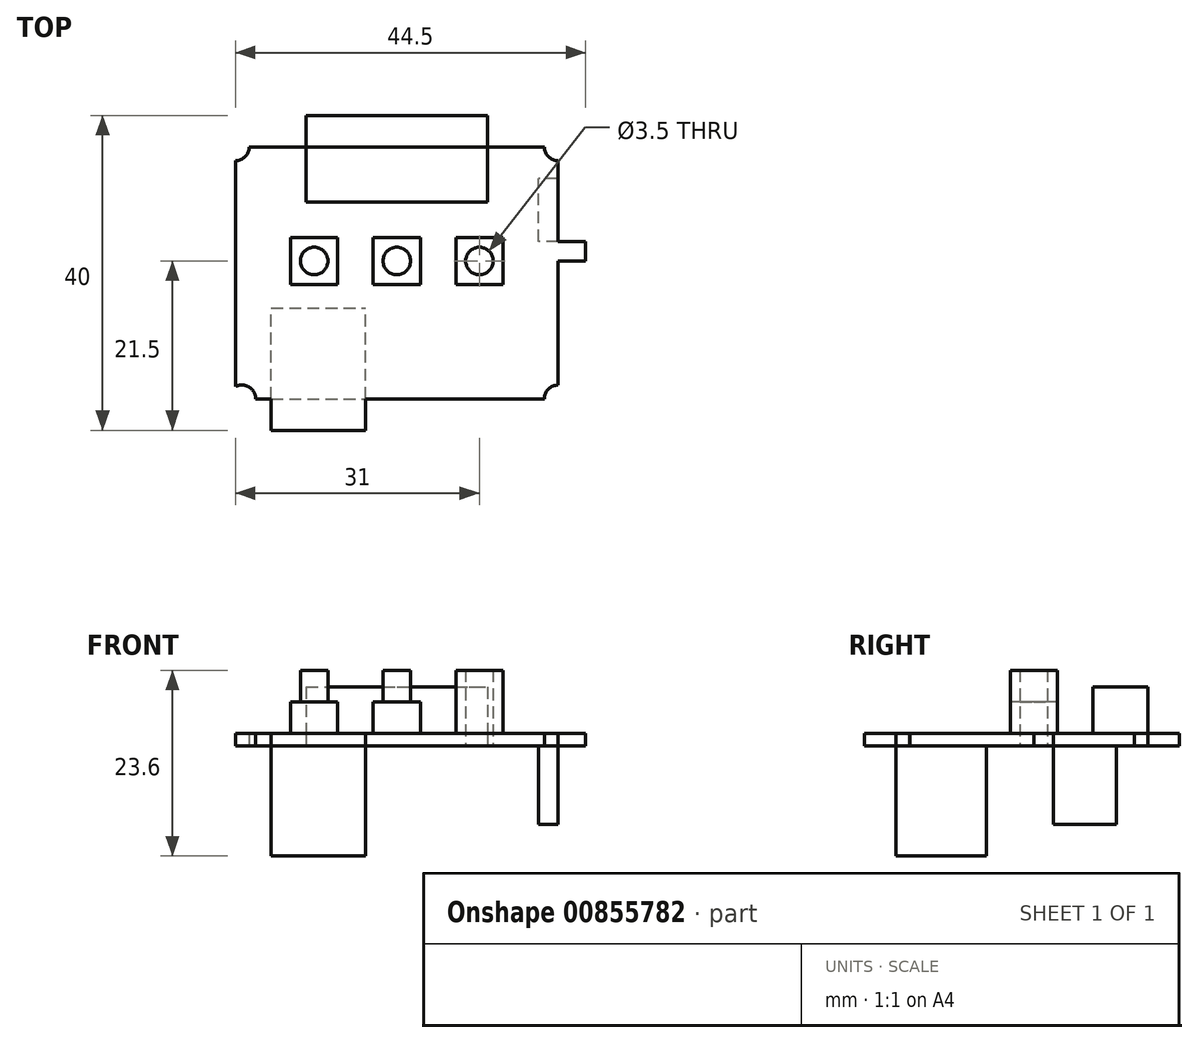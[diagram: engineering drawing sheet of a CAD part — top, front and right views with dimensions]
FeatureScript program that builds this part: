
annotation { "Feature Type Name" : "Feature", "Feature Type Description" : "" }
export const myFeature = defineFeature(function(context is Context, id is Id, definition is map)
    precondition{}
    {
        {
            var Q0;
            Q0=qCreatedBy(makeId("Top.planeOp"),FACE);
            var sketch = newSketch(context, id + "F0", { "sketchPlane" : qUnion([Q0])});
            skLineSegment(sketch, "E0.bottom", {"start": v(-20.5, 16) * mm, "end": v(20.5, 16) * mm});
            skLineSegment(sketch, "E0.top", {"start": v(-20.5, -16) * mm, "end": v(20.5, -16) * mm});
            skLineSegment(sketch, "E0.left", {"start": v(-20.5, 16) * mm, "end": v(-20.5, -16) * mm});
            skLineSegment(sketch, "E0.right", {"start": v(20.5, 16) * mm, "end": v(20.5, -16) * mm});
            skPoint(sketch, "E0.middle", {"position": v(0, 0) * mm});
            skLineSegment(sketch, "E1.bottom", {"start": v(-24, 20) * mm, "end": v(24, 20) * mm});
            skLineSegment(sketch, "E1.top", {"start": v(-24, -20) * mm, "end": v(24, -20) * mm});
            skLineSegment(sketch, "E1.left", {"start": v(-24, 20) * mm, "end": v(-24, -20) * mm});
            skLineSegment(sketch, "E1.right", {"start": v(24, 20) * mm, "end": v(24, -20) * mm});
            skCircle(sketch, "E2", {"center": v(-20.5, 16) * mm, "radius": 1.75 * mm});
            skCircle(sketch, "E3", {"center": v(20.5, 16) * mm, "radius": 1.75 * mm});
            skCircle(sketch, "E4", {"center": v(20.5, -16) * mm, "radius": 1.75 * mm});
            skCircle(sketch, "E5", {"center": v(-19.68, -16) * mm, "radius": 1.75 * mm});
            skLineSegment(sketch, "E6.bottom", {"start": v(-11.5, 20) * mm, "end": v(11.5, 20) * mm});
            skLineSegment(sketch, "E6.top", {"start": v(-11.5, 9) * mm, "end": v(11.5, 9) * mm});
            skLineSegment(sketch, "E6.left", {"start": v(-11.5, 20) * mm, "end": v(-11.5, 9) * mm});
            skLineSegment(sketch, "E6.right", {"start": v(11.5, 20) * mm, "end": v(11.5, 9) * mm});
            skLineSegment(sketch, "E7", {"start": v(-24, 1.5) * mm, "end": v(24, 1.5) * mm});
            skCircle(sketch, "E8", {"center": v(0, 1.5) * mm, "radius": 1.75 * mm});
            skCircle(sketch, "E9", {"center": v(-10.5, 1.5) * mm, "radius": 1.75 * mm});
            skCircle(sketch, "E10", {"center": v(10.5, 1.5) * mm, "radius": 1.75 * mm});
            skLineSegment(sketch, "E11.bottom", {"start": v(-13.5, 4.5) * mm, "end": v(-7.5, 4.5) * mm});
            skLineSegment(sketch, "E11.top", {"start": v(-13.5, -1.5) * mm, "end": v(-7.5, -1.5) * mm});
            skLineSegment(sketch, "E11.left", {"start": v(-13.5, 4.5) * mm, "end": v(-13.5, -1.5) * mm});
            skLineSegment(sketch, "E11.right", {"start": v(-7.5, 4.5) * mm, "end": v(-7.5, -1.5) * mm});
            skLineSegment(sketch, "E12.bottom", {"start": v(-3, 4.5) * mm, "end": v(3, 4.5) * mm});
            skLineSegment(sketch, "E12.top", {"start": v(-3, -1.5) * mm, "end": v(3, -1.5) * mm});
            skLineSegment(sketch, "E12.left", {"start": v(-3, 4.5) * mm, "end": v(-3, -1.5) * mm});
            skLineSegment(sketch, "E12.right", {"start": v(3, 4.5) * mm, "end": v(3, -1.5) * mm});
            skLineSegment(sketch, "E13.bottom", {"start": v(7.5, 4.5) * mm, "end": v(13.5, 4.5) * mm});
            skLineSegment(sketch, "E13.top", {"start": v(7.5, -1.5) * mm, "end": v(13.5, -1.5) * mm});
            skLineSegment(sketch, "E13.left", {"start": v(7.5, 4.5) * mm, "end": v(7.5, -1.5) * mm});
            skLineSegment(sketch, "E13.right", {"start": v(13.5, 4.5) * mm, "end": v(13.5, -1.5) * mm});
            skLineSegment(sketch, "E14.bottom", {"start": v(-15.95, -20) * mm, "end": v(-3.95, -20) * mm});
            skLineSegment(sketch, "E14.top", {"start": v(-15.95, -4.5) * mm, "end": v(-3.95, -4.5) * mm});
            skLineSegment(sketch, "E14.left", {"start": v(-15.95, -20) * mm, "end": v(-15.95, -4.5) * mm});
            skLineSegment(sketch, "E14.right", {"start": v(-3.95, -20) * mm, "end": v(-3.95, -4.5) * mm});
            skLineSegment(sketch, "E15.bottom", {"start": v(24, 4) * mm, "end": v(18, 4) * mm});
            skLineSegment(sketch, "E15.top", {"start": v(24, 12) * mm, "end": v(18, 12) * mm});
            skLineSegment(sketch, "E15.left", {"start": v(24, 4) * mm, "end": v(24, 12) * mm});
            skLineSegment(sketch, "E15.right", {"start": v(18, 4) * mm, "end": v(18, 12) * mm});
            skSolve(sketch);
        }
        {
            var Q0;
            {var subQ5=sQuery(id+"F0.wireOp",EDGE,"E2");var subQ10=sQuery(id+"F0.wireOp",EDGE,"E0.bottom");var subQ15=makeQuery(id+"F0.imprint","INTERSECT",VERTEX,{"derivedFrom":[subQ10,subQ5]});Q0=makeQuery(id+"F0.imprint","IMPRINT",FACE,{"disambiguationData":[TD([[makeQuery(id+"F0.imprint","IMPRINT",EDGE,{"disambiguationData":[TD([[subQ15,-1.0]])],"derivedFrom":subQ10}),-1.0]])]});}
            var Q1;
            Q1=makeQuery(id+"F0.imprint","IMPRINT",FACE,{"disambiguationData":[TD([[makeQuery(id+"F0.imprint","IMPRINT",EDGE,{"derivedFrom":sQuery(id+"F0.wireOp",EDGE,"E1.bottom")}),-1.0]])]});
            var Q2;
            {var subQ0=sQuery(id+"F0.wireOp",EDGE,"E11.top");Q2=makeQuery(id+"F0.imprint","IMPRINT",FACE,{"disambiguationData":[TD([[makeQuery(id+"F0.imprint","IMPRINT",EDGE,{"derivedFrom":subQ0}),-1.0]])]});}
            var Q3;
            {var subQ0=sQuery(id+"F0.wireOp",EDGE,"E1.top");Q3=makeQuery(id+"F0.imprint","IMPRINT",FACE,{"disambiguationData":[TD([[makeQuery(id+"F0.imprint","IMPRINT",EDGE,{"derivedFrom":subQ0}),1.0]])]});}
            var Q4;
            {var subQ5=sQuery(id+"F0.wireOp",EDGE,"E14.top");Q4=makeQuery(id+"F0.imprint","IMPRINT",FACE,{"disambiguationData":[TD([[makeQuery(id+"F0.imprint","IMPRINT",EDGE,{"derivedFrom":subQ5}),-1.0]])]});}
            var Q5;
            {var subQ5=sQuery(id+"F0.wireOp",EDGE,"E14.bottom");Q5=makeQuery(id+"F0.imprint","IMPRINT",FACE,{"disambiguationData":[TD([[makeQuery(id+"F0.imprint","IMPRINT",EDGE,{"derivedFrom":subQ5}),1.0]])]});}
            var Q6;
            {var subQ5=sQuery(id+"F0.wireOp",EDGE,"E15.left");Q6=makeQuery(id+"F0.imprint","IMPRINT",FACE,{"disambiguationData":[TD([[makeQuery(id+"F0.imprint","IMPRINT",EDGE,{"derivedFrom":subQ5}),1.0]])]});}
            var Q7;
            {var subQ0=sQuery(id+"F0.wireOp",EDGE,"E15.bottom");var subQ1=sQuery(id+"F0.wireOp",EDGE,"E0.right");var subQ2=makeQuery(id+"F0.imprint","INTERSECT",VERTEX,{"derivedFrom":[subQ1,subQ0]});Q7=makeQuery(id+"F0.imprint","IMPRINT",FACE,{"disambiguationData":[TD([[makeQuery(id+"F0.imprint","IMPRINT",EDGE,{"disambiguationData":[TD([[subQ2,-1.0]])],"derivedFrom":subQ1}),1.0]])]});}
            var Q8;
            {var subQ5=sQuery(id+"F0.wireOp",EDGE,"E15.right");Q8=makeQuery(id+"F0.imprint","IMPRINT",FACE,{"disambiguationData":[TD([[makeQuery(id+"F0.imprint","IMPRINT",EDGE,{"derivedFrom":subQ5}),-1.0]])]});}
            var Q9;
            {var subQ0=sQuery(id+"F0.wireOp",EDGE,"E11.bottom");Q9=makeQuery(id+"F0.imprint","IMPRINT",FACE,{"disambiguationData":[TD([[makeQuery(id+"F0.imprint","IMPRINT",EDGE,{"derivedFrom":subQ0}),-1.0]])]});}
            var Q10;
            {var subQ0=sQuery(id+"F0.wireOp",EDGE,"E12.bottom");Q10=makeQuery(id+"F0.imprint","IMPRINT",FACE,{"disambiguationData":[TD([[makeQuery(id+"F0.imprint","IMPRINT",EDGE,{"derivedFrom":subQ0}),-1.0]])]});}
            var Q11;
            {var subQ0=sQuery(id+"F0.wireOp",EDGE,"E13.bottom");Q11=makeQuery(id+"F0.imprint","IMPRINT",FACE,{"disambiguationData":[TD([[makeQuery(id+"F0.imprint","IMPRINT",EDGE,{"derivedFrom":subQ0}),-1.0]])]});}
            var Q12;
            {var subQ0=sQuery(id+"F0.wireOp",EDGE,"E9");var subQ1=sQuery(id+"F0.wireOp",EDGE,"E7");var subQ2=makeQuery(id+"F0.imprint","INTERSECT",VERTEX,{"disambiguationData":[OD(0.0)],"derivedFrom":[subQ1,subQ0]});Q12=makeQuery(id+"F0.imprint","IMPRINT",FACE,{"disambiguationData":[TD([[makeQuery(id+"F0.imprint","IMPRINT",EDGE,{"disambiguationData":[TD([[subQ2,-1.0]])],"derivedFrom":subQ1}),1.0]])]});}
            var Q13;
            {var subQ0=sQuery(id+"F0.wireOp",EDGE,"E9");var subQ1=sQuery(id+"F0.wireOp",EDGE,"E7");var subQ2=makeQuery(id+"F0.imprint","INTERSECT",VERTEX,{"disambiguationData":[OD(0.0)],"derivedFrom":[subQ1,subQ0]});Q13=makeQuery(id+"F0.imprint","IMPRINT",FACE,{"disambiguationData":[TD([[makeQuery(id+"F0.imprint","IMPRINT",EDGE,{"disambiguationData":[TD([[subQ2,-1.0]])],"derivedFrom":subQ1}),-1.0]])]});}
            var Q14;
            {var subQ6=sQuery(id+"F0.wireOp",EDGE,"E11.top");Q14=makeQuery(id+"F0.imprint","IMPRINT",FACE,{"disambiguationData":[TD([[makeQuery(id+"F0.imprint","IMPRINT",EDGE,{"derivedFrom":subQ6}),1.0]])]});}
            var Q15;
            {var subQ0=sQuery(id+"F0.wireOp",EDGE,"E12.top");Q15=makeQuery(id+"F0.imprint","IMPRINT",FACE,{"disambiguationData":[TD([[makeQuery(id+"F0.imprint","IMPRINT",EDGE,{"derivedFrom":subQ0}),1.0]])]});}
            var Q16;
            {var subQ0=sQuery(id+"F0.wireOp",EDGE,"E8");var subQ1=sQuery(id+"F0.wireOp",EDGE,"E7");var subQ2=makeQuery(id+"F0.imprint","INTERSECT",VERTEX,{"disambiguationData":[OD(0.0)],"derivedFrom":[subQ1,subQ0]});Q16=makeQuery(id+"F0.imprint","IMPRINT",FACE,{"disambiguationData":[TD([[makeQuery(id+"F0.imprint","IMPRINT",EDGE,{"disambiguationData":[TD([[subQ2,-1.0]])],"derivedFrom":subQ1}),-1.0]])]});}
            var Q17;
            {var subQ0=sQuery(id+"F0.wireOp",EDGE,"E8");var subQ1=sQuery(id+"F0.wireOp",EDGE,"E7");var subQ2=makeQuery(id+"F0.imprint","INTERSECT",VERTEX,{"disambiguationData":[OD(0.0)],"derivedFrom":[subQ1,subQ0]});Q17=makeQuery(id+"F0.imprint","IMPRINT",FACE,{"disambiguationData":[TD([[makeQuery(id+"F0.imprint","IMPRINT",EDGE,{"disambiguationData":[TD([[subQ2,-1.0]])],"derivedFrom":subQ1}),1.0]])]});}
            var Q18;
            {var subQ0=sQuery(id+"F0.wireOp",EDGE,"E10");var subQ1=sQuery(id+"F0.wireOp",EDGE,"E7");var subQ2=makeQuery(id+"F0.imprint","INTERSECT",VERTEX,{"disambiguationData":[OD(0.0)],"derivedFrom":[subQ1,subQ0]});Q18=makeQuery(id+"F0.imprint","IMPRINT",FACE,{"disambiguationData":[TD([[makeQuery(id+"F0.imprint","IMPRINT",EDGE,{"disambiguationData":[TD([[subQ2,-1.0]])],"derivedFrom":subQ1}),1.0]])]});}
            var Q19;
            {var subQ0=sQuery(id+"F0.wireOp",EDGE,"E10");var subQ1=sQuery(id+"F0.wireOp",EDGE,"E7");var subQ2=makeQuery(id+"F0.imprint","INTERSECT",VERTEX,{"disambiguationData":[OD(0.0)],"derivedFrom":[subQ1,subQ0]});Q19=makeQuery(id+"F0.imprint","IMPRINT",FACE,{"disambiguationData":[TD([[makeQuery(id+"F0.imprint","IMPRINT",EDGE,{"disambiguationData":[TD([[subQ2,-1.0]])],"derivedFrom":subQ1}),-1.0]])]});}
            var Q20;
            {var subQ0=sQuery(id+"F0.wireOp",EDGE,"E13.top");Q20=makeQuery(id+"F0.imprint","IMPRINT",FACE,{"disambiguationData":[TD([[makeQuery(id+"F0.imprint","IMPRINT",EDGE,{"derivedFrom":subQ0}),1.0]])]});}
            extrude(context, id + "F1", {"entities" : qUnion([Q0, Q1, Q2, Q3, Q4, Q5, Q6, Q7, Q8, Q9, Q10, Q11, Q12, Q13, Q14, Q15, Q16, Q17, Q18, Q19, Q20]), "depth" : 1.6 * mm, "offsetDistance" : 25 * mm});
        }
        {
            var Q0;
            {var subQ5=sQuery(id+"F0.wireOp",EDGE,"E6.top");Q0=makeQuery(id+"F0.imprint","IMPRINT",FACE,{"disambiguationData":[TD([[makeQuery(id+"F0.imprint","IMPRINT",EDGE,{"derivedFrom":subQ5}),1.0]])]});}
            var Q1;
            {var subQ5=sQuery(id+"F0.wireOp",EDGE,"E6.bottom");Q1=makeQuery(id+"F0.imprint","IMPRINT",FACE,{"disambiguationData":[TD([[makeQuery(id+"F0.imprint","IMPRINT",EDGE,{"derivedFrom":subQ5}),-1.0]])]});}
            extrude(context, id + "F2", {"entities" : qUnion([Q0, Q1]), "operationType" : NewBodyOperationType.ADD, "depth" : 7.5 * mm, "offsetDistance" : 25 * mm});
        }
        {
            var Q0;
            {var subQ0=sQuery(id+"F0.wireOp",EDGE,"E11.bottom");Q0=makeQuery(id+"F0.imprint","IMPRINT",FACE,{"disambiguationData":[TD([[makeQuery(id+"F0.imprint","IMPRINT",EDGE,{"derivedFrom":subQ0}),-1.0]])]});}
            var Q1;
            {var subQ6=sQuery(id+"F0.wireOp",EDGE,"E11.top");Q1=makeQuery(id+"F0.imprint","IMPRINT",FACE,{"disambiguationData":[TD([[makeQuery(id+"F0.imprint","IMPRINT",EDGE,{"derivedFrom":subQ6}),1.0]])]});}
            var Q2;
            {var subQ0=sQuery(id+"F0.wireOp",EDGE,"E12.bottom");Q2=makeQuery(id+"F0.imprint","IMPRINT",FACE,{"disambiguationData":[TD([[makeQuery(id+"F0.imprint","IMPRINT",EDGE,{"derivedFrom":subQ0}),-1.0]])]});}
            var Q3;
            {var subQ0=sQuery(id+"F0.wireOp",EDGE,"E12.top");Q3=makeQuery(id+"F0.imprint","IMPRINT",FACE,{"disambiguationData":[TD([[makeQuery(id+"F0.imprint","IMPRINT",EDGE,{"derivedFrom":subQ0}),1.0]])]});}
            var Q4;
            {var subQ0=sQuery(id+"F0.wireOp",EDGE,"E13.bottom");Q4=makeQuery(id+"F0.imprint","IMPRINT",FACE,{"disambiguationData":[TD([[makeQuery(id+"F0.imprint","IMPRINT",EDGE,{"derivedFrom":subQ0}),-1.0]])]});}
            var Q5;
            {var subQ0=sQuery(id+"F0.wireOp",EDGE,"E13.top");Q5=makeQuery(id+"F0.imprint","IMPRINT",FACE,{"disambiguationData":[TD([[makeQuery(id+"F0.imprint","IMPRINT",EDGE,{"derivedFrom":subQ0}),1.0]])]});}
            extrude(context, id + "F3", {"entities" : qUnion([Q0, Q1, Q2, Q3, Q4, Q5]), "operationType" : NewBodyOperationType.ADD, "depth" : 5.6 * mm, "offsetDistance" : 25 * mm});
        }
        {
            var Q0;
            {var subQ0=sQuery(id+"F0.wireOp",EDGE,"E8");var subQ1=sQuery(id+"F0.wireOp",EDGE,"E7");var subQ2=makeQuery(id+"F0.imprint","INTERSECT",VERTEX,{"disambiguationData":[OD(0.0)],"derivedFrom":[subQ1,subQ0]});Q0=makeQuery(id+"F0.imprint","IMPRINT",FACE,{"disambiguationData":[TD([[makeQuery(id+"F0.imprint","IMPRINT",EDGE,{"disambiguationData":[TD([[subQ2,-1.0]])],"derivedFrom":subQ1}),1.0]])]});}
            var Q1;
            {var subQ0=sQuery(id+"F0.wireOp",EDGE,"E8");var subQ1=sQuery(id+"F0.wireOp",EDGE,"E7");var subQ2=makeQuery(id+"F0.imprint","INTERSECT",VERTEX,{"disambiguationData":[OD(0.0)],"derivedFrom":[subQ1,subQ0]});Q1=makeQuery(id+"F0.imprint","IMPRINT",FACE,{"disambiguationData":[TD([[makeQuery(id+"F0.imprint","IMPRINT",EDGE,{"disambiguationData":[TD([[subQ2,-1.0]])],"derivedFrom":subQ1}),-1.0]])]});}
            var Q2;
            {var subQ0=sQuery(id+"F0.wireOp",EDGE,"E9");var subQ1=sQuery(id+"F0.wireOp",EDGE,"E7");var subQ2=makeQuery(id+"F0.imprint","INTERSECT",VERTEX,{"disambiguationData":[OD(0.0)],"derivedFrom":[subQ1,subQ0]});Q2=makeQuery(id+"F0.imprint","IMPRINT",FACE,{"disambiguationData":[TD([[makeQuery(id+"F0.imprint","IMPRINT",EDGE,{"disambiguationData":[TD([[subQ2,-1.0]])],"derivedFrom":subQ1}),1.0]])]});}
            var Q3;
            {var subQ0=sQuery(id+"F0.wireOp",EDGE,"E9");var subQ1=sQuery(id+"F0.wireOp",EDGE,"E7");var subQ2=makeQuery(id+"F0.imprint","INTERSECT",VERTEX,{"disambiguationData":[OD(0.0)],"derivedFrom":[subQ1,subQ0]});Q3=makeQuery(id+"F0.imprint","IMPRINT",FACE,{"disambiguationData":[TD([[makeQuery(id+"F0.imprint","IMPRINT",EDGE,{"disambiguationData":[TD([[subQ2,-1.0]])],"derivedFrom":subQ1}),-1.0]])]});}
            var Q4;
            {var subQ0=sQuery(id+"F0.wireOp",EDGE,"E10");var subQ1=sQuery(id+"F0.wireOp",EDGE,"E7");var subQ2=makeQuery(id+"F0.imprint","INTERSECT",VERTEX,{"disambiguationData":[OD(0.0)],"derivedFrom":[subQ1,subQ0]});Q4=makeQuery(id+"F0.imprint","IMPRINT",FACE,{"disambiguationData":[TD([[makeQuery(id+"F0.imprint","IMPRINT",EDGE,{"disambiguationData":[TD([[subQ2,-1.0]])],"derivedFrom":subQ1}),1.0]])]});}
            var Q5;
            {var subQ0=sQuery(id+"F0.wireOp",EDGE,"E10");var subQ1=sQuery(id+"F0.wireOp",EDGE,"E7");var subQ2=makeQuery(id+"F0.imprint","INTERSECT",VERTEX,{"disambiguationData":[OD(0.0)],"derivedFrom":[subQ1,subQ0]});Q5=makeQuery(id+"F0.imprint","IMPRINT",FACE,{"disambiguationData":[TD([[makeQuery(id+"F0.imprint","IMPRINT",EDGE,{"disambiguationData":[TD([[subQ2,-1.0]])],"derivedFrom":subQ1}),-1.0]])]});}
            extrude(context, id + "F4", {"entities" : qUnion([Q0, Q1, Q2, Q3, Q4, Q5]), "operationType" : NewBodyOperationType.ADD, "depth" : 9.6 * mm, "offsetDistance" : 25 * mm});
        }
        {
            var Q0;
            {var subQ5=sQuery(id+"F0.wireOp",EDGE,"E14.top");Q0=makeQuery(id+"F0.imprint","IMPRINT",FACE,{"disambiguationData":[TD([[makeQuery(id+"F0.imprint","IMPRINT",EDGE,{"derivedFrom":subQ5}),-1.0]])]});}
            var Q1;
            {var subQ5=sQuery(id+"F0.wireOp",EDGE,"E14.bottom");Q1=makeQuery(id+"F0.imprint","IMPRINT",FACE,{"disambiguationData":[TD([[makeQuery(id+"F0.imprint","IMPRINT",EDGE,{"derivedFrom":subQ5}),1.0]])]});}
            extrude(context, id + "F5", {"entities" : qUnion([Q0, Q1]), "oppositeDirection" : true, "depth" : 14 * mm, "offsetDistance" : 25 * mm});
        }
        {
            var Q0;
            {var subQ5=sQuery(id+"F0.wireOp",EDGE,"E15.left");Q0=makeQuery(id+"F0.imprint","IMPRINT",FACE,{"disambiguationData":[TD([[makeQuery(id+"F0.imprint","IMPRINT",EDGE,{"derivedFrom":subQ5}),1.0]])]});}
            var Q1;
            {var subQ5=sQuery(id+"F0.wireOp",EDGE,"E15.right");Q1=makeQuery(id+"F0.imprint","IMPRINT",FACE,{"disambiguationData":[TD([[makeQuery(id+"F0.imprint","IMPRINT",EDGE,{"derivedFrom":subQ5}),-1.0]])]});}
            extrude(context, id + "F6", {"entities" : qUnion([Q0, Q1]), "oppositeDirection" : true, "depth" : 10 * mm, "offsetDistance" : 25 * mm});
        }
    });
